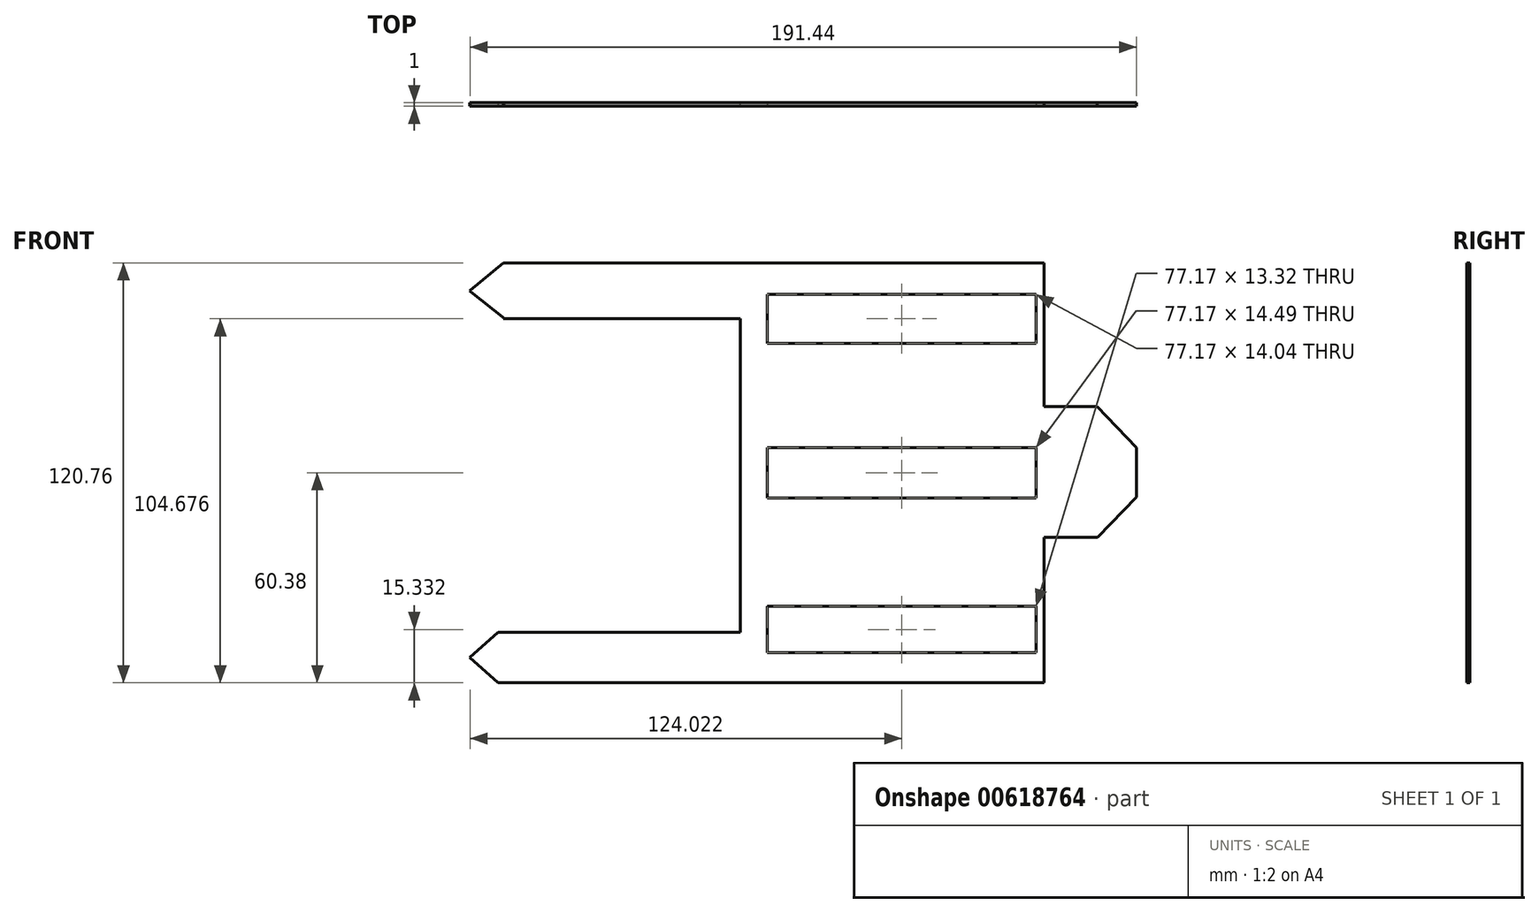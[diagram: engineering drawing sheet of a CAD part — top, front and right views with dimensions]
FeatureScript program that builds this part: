
annotation { "Feature Type Name" : "Feature", "Feature Type Description" : "" }
export const myFeature = defineFeature(function(context is Context, id is Id, definition is map)
    precondition{}
    {
        {
            var Q0;
            Q0=qCreatedBy(makeId("Front.planeOp"),FACE);
            var sketch = newSketch(context, id + "F0", { "sketchPlane" : qUnion([Q0])});
            skLineSegment(sketch, "E0.bottom", {"start": v(95.72, 60.38) * mm, "end": v(-95.72, 60.38) * mm});
            skLineSegment(sketch, "E0.top", {"start": v(95.72, -60.38) * mm, "end": v(-95.72, -60.38) * mm});
            skLineSegment(sketch, "E0.left", {"start": v(95.72, 60.38) * mm, "end": v(95.72, -60.38) * mm});
            skLineSegment(sketch, "E0.right", {"start": v(-95.72, 60.38) * mm, "end": v(-95.72, -60.38) * mm});
            skPoint(sketch, "E0.middle", {"position": v(0, 0) * mm});
            skLineSegment(sketch, "E1", {"start": v(-95.72, 44.3) * mm, "end": v(-18.05, 44.3) * mm});
            skLineSegment(sketch, "E2", {"start": v(-18.05, 44.3) * mm, "end": v(-18.05, -45.81) * mm});
            skLineSegment(sketch, "E3", {"start": v(-18.05, -45.81) * mm, "end": v(-95.72, -45.81) * mm});
            skLineSegment(sketch, "E4", {"start": v(-95.72, -45.81) * mm, "end": v(-95.72, -60.38) * mm});
            skLineSegment(sketch, "E5", {"start": v(-95.72, 44.3) * mm, "end": v(-95.72, 60.38) * mm});
            skLineSegment(sketch, "E6", {"start": v(-95.72, -45.81) * mm, "end": v(-95.72, 44.3) * mm});
            skSolve(sketch);
        }
        {
            var Q0;
            {var subQ1=sQuery(id+"F0.wireOp",EDGE,"E0.bottom");Q0=makeQuery(id+"F0.imprint","IMPRINT",FACE,{"disambiguationData":[TD([[makeQuery(id+"F0.imprint","IMPRINT",EDGE,{"derivedFrom":subQ1}),1.0]])]});}
            extrude(context, id + "F1", {"entities" : qUnion([Q0]), "depth" : 1 * mm, "offsetDistance" : 25.4 * mm});
        }
        {
            var Q0;
            Q0=makeQuery(id+"F1.opExtrude","CAP_FACE",FACE,{"disambiguationData":[OSD([sQuery(id+"F0.wireOp",EDGE,"E0.bottom"),sQuery(id+"F0.wireOp",EDGE,"E0.top"),sQuery(id+"F0.wireOp",EDGE,"E0.left"),sQuery(id+"F0.wireOp",EDGE,"E0.right"),sQuery(id+"F0.wireOp",EDGE,"E1"),sQuery(id+"F0.wireOp",EDGE,"E2"),sQuery(id+"F0.wireOp",EDGE,"E3")])],"isStart":false});
            var sketch = newSketch(context, id + "F2", { "sketchPlane" : qUnion([Q0])});
            skLineSegment(sketch, "E7.bottom", {"start": v(66.89, 7.25) * mm, "end": v(-10.28, 7.25) * mm});
            skLineSegment(sketch, "E7.top", {"start": v(66.89, -7.25) * mm, "end": v(-10.28, -7.25) * mm});
            skLineSegment(sketch, "E7.left", {"start": v(66.89, 7.25) * mm, "end": v(66.89, -7.25) * mm});
            skLineSegment(sketch, "E7.right", {"start": v(-10.28, 7.25) * mm, "end": v(-10.28, -7.25) * mm});
            skPoint(sketch, "E7.middle", {"position": v(28.3, 0) * mm});
            skLineSegment(sketch, "E8.bottom", {"start": v(66.89, -38.39) * mm, "end": v(-10.28, -38.39) * mm});
            skLineSegment(sketch, "E8.top", {"start": v(66.89, -51.7) * mm, "end": v(-10.28, -51.7) * mm});
            skLineSegment(sketch, "E8.left", {"start": v(66.89, -38.39) * mm, "end": v(66.89, -51.7) * mm});
            skLineSegment(sketch, "E8.right", {"start": v(-10.28, -38.39) * mm, "end": v(-10.28, -51.7) * mm});
            skPoint(sketch, "E8.middle", {"position": v(28.3, -45.05) * mm});
            skLineSegment(sketch, "E9.bottom", {"start": v(66.89, 51.32) * mm, "end": v(-10.28, 51.32) * mm});
            skLineSegment(sketch, "E9.top", {"start": v(66.89, 37.28) * mm, "end": v(-10.28, 37.28) * mm});
            skLineSegment(sketch, "E9.left", {"start": v(66.89, 51.32) * mm, "end": v(66.89, 37.28) * mm});
            skLineSegment(sketch, "E9.right", {"start": v(-10.28, 51.32) * mm, "end": v(-10.28, 37.28) * mm});
            skPoint(sketch, "E9.middle", {"position": v(28.3, 44.3) * mm});
            skPoint(sketch, "E9.middle.positionSnap0", {"position": v(28.3, 7.25) * mm});
            skPoint(sketch, "E9.centerSnap0", {"position": v(28.3, 7.25) * mm});
            skSolve(sketch);
        }
        {
            var Q0;
            Q0=makeQuery(id+"F2.imprint","IMPRINT",FACE,{"disambiguationData":[TD([[makeQuery(id+"F2.imprint","IMPRINT",EDGE,{"derivedFrom":sQuery(id+"F2.wireOp",EDGE,"E9.bottom")}),1.0]])]});
            var Q1;
            Q1=makeQuery(id+"F2.imprint","IMPRINT",FACE,{"disambiguationData":[TD([[makeQuery(id+"F2.imprint","IMPRINT",EDGE,{"derivedFrom":sQuery(id+"F2.wireOp",EDGE,"E7.bottom")}),1.0]])]});
            var Q2;
            Q2=makeQuery(id+"F2.imprint","IMPRINT",FACE,{"disambiguationData":[TD([[makeQuery(id+"F2.imprint","IMPRINT",EDGE,{"derivedFrom":sQuery(id+"F2.wireOp",EDGE,"E8.bottom")}),1.0]])]});
            extrude(context, id + "F3", {"entities" : qUnion([Q0, Q1, Q2]), "operationType" : NewBodyOperationType.REMOVE, "oppositeDirection" : true, "depth" : 25.4 * mm, "offsetDistance" : 25.4 * mm});
        }
        {
            var Q0;
            Q0=makeQuery(id+"F1.opExtrude","CAP_FACE",FACE,{"disambiguationData":[OSD([sQuery(id+"F0.wireOp",EDGE,"E0.bottom"),sQuery(id+"F0.wireOp",EDGE,"E0.top"),sQuery(id+"F0.wireOp",EDGE,"E0.left"),sQuery(id+"F0.wireOp",EDGE,"E0.right"),sQuery(id+"F0.wireOp",EDGE,"E1"),sQuery(id+"F0.wireOp",EDGE,"E2"),sQuery(id+"F0.wireOp",EDGE,"E3")])],"isStart":false});
            var sketch = newSketch(context, id + "F4", { "sketchPlane" : qUnion([Q0])});
            skLineSegment(sketch, "E10", {"start": v(69.14, 0) * mm, "end": v(69.14, -18.59) * mm});
            skLineSegment(sketch, "E11", {"start": v(69.14, -18.59) * mm, "end": v(84.5, -18.59) * mm});
            skLineSegment(sketch, "E12", {"start": v(69.14, 0) * mm, "end": v(69.14, 19.07) * mm});
            skLineSegment(sketch, "E13", {"start": v(69.14, 19.07) * mm, "end": v(84.46, 19.07) * mm});
            skLineSegment(sketch, "E14", {"start": v(84.46, 19.07) * mm, "end": v(95.72, 7.22) * mm});
            skLineSegment(sketch, "E15", {"start": v(95.72, 7.22) * mm, "end": v(95.72, -7) * mm});
            skLineSegment(sketch, "E16", {"start": v(95.72, -7) * mm, "end": v(84.5, -18.59) * mm});
            skLineSegment(sketch, "E17", {"start": v(69.14, 19.07) * mm, "end": v(69.14, 60.38) * mm});
            skLineSegment(sketch, "E18", {"start": v(69.14, 60.38) * mm, "end": v(95.72, 60.38) * mm});
            skLineSegment(sketch, "E19", {"start": v(95.72, 60.38) * mm, "end": v(95.72, 7.22) * mm});
            skLineSegment(sketch, "E20", {"start": v(69.14, -18.59) * mm, "end": v(69.14, -60.38) * mm});
            skLineSegment(sketch, "E21", {"start": v(69.14, -60.38) * mm, "end": v(95.72, -60.38) * mm});
            skLineSegment(sketch, "E22", {"start": v(95.72, -60.38) * mm, "end": v(95.72, -7) * mm});
            skSolve(sketch);
        }
        {
            var Q0;
            Q0=makeQuery(id+"F4.imprint","IMPRINT",FACE,{"disambiguationData":[TD([[makeQuery(id+"F4.imprint","IMPRINT",EDGE,{"derivedFrom":sQuery(id+"F4.wireOp",EDGE,"E11")}),-1.0]])]});
            var Q1;
            Q1=makeQuery(id+"F4.imprint","IMPRINT",FACE,{"disambiguationData":[TD([[makeQuery(id+"F4.imprint","IMPRINT",EDGE,{"derivedFrom":sQuery(id+"F4.wireOp",EDGE,"E13")}),1.0]])]});
            extrude(context, id + "F5", {"entities" : qUnion([Q0, Q1]), "operationType" : NewBodyOperationType.REMOVE, "oppositeDirection" : true, "depth" : 25.4 * mm, "offsetDistance" : 25.4 * mm});
        }
        {
            var Q0;
            Q0=makeQuery(id+"F1.opExtrude","CAP_FACE",FACE,{"disambiguationData":[OSD([sQuery(id+"F0.wireOp",EDGE,"E0.bottom"),sQuery(id+"F0.wireOp",EDGE,"E0.top"),sQuery(id+"F0.wireOp",EDGE,"E0.left"),sQuery(id+"F0.wireOp",EDGE,"E0.right"),sQuery(id+"F0.wireOp",EDGE,"E1"),sQuery(id+"F0.wireOp",EDGE,"E2"),sQuery(id+"F0.wireOp",EDGE,"E3")])],"isStart":false});
            var sketch = newSketch(context, id + "F6", { "sketchPlane" : qUnion([Q0])});
            skLineSegment(sketch, "E23", {"start": v(-95.72, 52.34) * mm, "end": v(-88.4, 60.38) * mm});
            skLineSegment(sketch, "E24", {"start": v(-88.4, 60.38) * mm, "end": v(-88.4, 44.3) * mm});
            skLineSegment(sketch, "E25", {"start": v(-88.4, 44.3) * mm, "end": v(-95.72, 52.34) * mm});
            skLineSegment(sketch, "E26", {"start": v(-95.72, 52.34) * mm, "end": v(-95.72, 44.3) * mm});
            skLineSegment(sketch, "E27", {"start": v(-95.72, 44.3) * mm, "end": v(-88.4, 44.3) * mm});
            skLineSegment(sketch, "E28", {"start": v(-88.4, 60.38) * mm, "end": v(-95.72, 60.38) * mm});
            skLineSegment(sketch, "E29", {"start": v(-95.72, 60.38) * mm, "end": v(-95.72, 52.34) * mm});
            skSolve(sketch);
        }
        {
            var Q0;
            Q0=makeQuery(id+"F6.imprint","IMPRINT",FACE,{"disambiguationData":[TD([[makeQuery(id+"F6.imprint","IMPRINT",EDGE,{"derivedFrom":sQuery(id+"F6.wireOp",EDGE,"E23")}),1.0]])]});
            var Q1;
            Q1=makeQuery(id+"F6.imprint","IMPRINT",FACE,{"disambiguationData":[TD([[makeQuery(id+"F6.imprint","IMPRINT",EDGE,{"derivedFrom":sQuery(id+"F6.wireOp",EDGE,"E25")}),1.0]])]});
            extrude(context, id + "F7", {"entities" : qUnion([Q0, Q1]), "operationType" : NewBodyOperationType.REMOVE, "oppositeDirection" : true, "depth" : 25.4 * mm, "offsetDistance" : 25.4 * mm});
        }
        {
            var Q0;
            Q0=makeQuery(id+"F1.opExtrude","CAP_FACE",FACE,{"disambiguationData":[OSD([sQuery(id+"F0.wireOp",EDGE,"E0.bottom"),sQuery(id+"F0.wireOp",EDGE,"E0.top"),sQuery(id+"F0.wireOp",EDGE,"E0.left"),sQuery(id+"F0.wireOp",EDGE,"E0.right"),sQuery(id+"F0.wireOp",EDGE,"E1"),sQuery(id+"F0.wireOp",EDGE,"E2"),sQuery(id+"F0.wireOp",EDGE,"E3")])],"isStart":false});
            var sketch = newSketch(context, id + "F8", { "sketchPlane" : qUnion([Q0])});
            skLineSegment(sketch, "E30", {"start": v(-95.72, -53.1) * mm, "end": v(-87.66, -45.81) * mm});
            skLineSegment(sketch, "E31", {"start": v(-87.66, -45.81) * mm, "end": v(-87.66, -60.38) * mm});
            skLineSegment(sketch, "E32", {"start": v(-87.66, -60.38) * mm, "end": v(-95.72, -53.1) * mm});
            skLineSegment(sketch, "E33", {"start": v(-87.66, -45.81) * mm, "end": v(-95.72, -45.81) * mm});
            skLineSegment(sketch, "E34", {"start": v(-95.72, -45.81) * mm, "end": v(-95.72, -53.1) * mm});
            skLineSegment(sketch, "E35", {"start": v(-87.66, -60.38) * mm, "end": v(-95.72, -60.38) * mm});
            skLineSegment(sketch, "E36", {"start": v(-95.72, -60.38) * mm, "end": v(-95.72, -53.1) * mm});
            skSolve(sketch);
        }
        {
            var Q0;
            Q0=makeQuery(id+"F8.imprint","IMPRINT",FACE,{"disambiguationData":[TD([[makeQuery(id+"F8.imprint","IMPRINT",EDGE,{"derivedFrom":sQuery(id+"F8.wireOp",EDGE,"E30")}),1.0]])]});
            var Q1;
            Q1=makeQuery(id+"F8.imprint","IMPRINT",FACE,{"disambiguationData":[TD([[makeQuery(id+"F8.imprint","IMPRINT",EDGE,{"derivedFrom":sQuery(id+"F8.wireOp",EDGE,"E32")}),1.0]])]});
            extrude(context, id + "F9", {"entities" : qUnion([Q0, Q1]), "operationType" : NewBodyOperationType.REMOVE, "oppositeDirection" : true, "depth" : 25.4 * mm, "offsetDistance" : 25.4 * mm});
        }
        {
            var Q0;
            Q0=makeQuery(id+"F1.opExtrude","CAP_FACE",FACE,{"disambiguationData":[OSD([sQuery(id+"F0.wireOp",EDGE,"E0.bottom"),sQuery(id+"F0.wireOp",EDGE,"E0.top"),sQuery(id+"F0.wireOp",EDGE,"E0.left"),sQuery(id+"F0.wireOp",EDGE,"E0.right"),sQuery(id+"F0.wireOp",EDGE,"E1"),sQuery(id+"F0.wireOp",EDGE,"E2"),sQuery(id+"F0.wireOp",EDGE,"E3")])],"isStart":false});
            var sketch = newSketch(context, id + "F10", { "sketchPlane" : qUnion([Q0])});
            skLineSegment(sketch, "E37", {"start": v(-95.72, -53.1) * mm, "end": v(-87.66, -53.1) * mm});
            skLineSegment(sketch, "E38", {"start": v(-95.72, 52.34) * mm, "end": v(-87.61, 52.34) * mm});
            skSolve(sketch);
        }
        {
            var Q0;
            Q0=makeQuery(id+"F10.imprint","IMPRINT",FACE,{"disambiguationData":[TD([[makeQuery(id+"F10.imprint","IMPRINT",EDGE,{"derivedFrom":makeQuery(id+"F1.opExtrude","CAP_EDGE",EDGE,{"disambiguationData":[OSD([sQuery(id+"F0.wireOp",EDGE,"E2")])],"isStart":false})}),1.0]])]});
            var sketch = newSketch(context, id + "F11", { "sketchPlane" : qUnion([Q0])});
            skLineSegment(sketch, "E39", {"start": v(-96, 52.52) * mm, "end": v(-85.7, 44.32) * mm});
            skLineSegment(sketch, "E40", {"start": v(-85.7, 44.32) * mm, "end": v(-89.33, 44.32) * mm});
            skLineSegment(sketch, "E41", {"start": v(-89.33, 44.32) * mm, "end": v(-96, 52.52) * mm});
            skLineSegment(sketch, "E42", {"start": v(-96, 52.52) * mm, "end": v(-87.52, 59.44) * mm});
            skPoint(sketch, "E42.endSnap0", {"position": v(-87.52, 44.32) * mm});
            skLineSegment(sketch, "E43", {"start": v(-87.52, 59.44) * mm, "end": v(-89.33, 61.66) * mm});
            skLineSegment(sketch, "E44", {"start": v(-89.33, 61.66) * mm, "end": v(-96, 52.52) * mm});
            skSolve(sketch);
        }
        {
            var Q0;
            {var subQ0=sQuery(id+"F11.wireOp",EDGE,"E40");var subQ1=sQuery(id+"F11.wireOp",EDGE,"E39");var subQ2=makeQuery(id+"F11.imprint","INTERSECT",VERTEX,{"derivedFrom":[subQ1,subQ0]});Q0=makeQuery(id+"F11.imprint","IMPRINT",FACE,{"disambiguationData":[TD([[makeQuery(id+"F11.imprint","IMPRINT",EDGE,{"disambiguationData":[TD([[subQ2,1.0]])],"derivedFrom":subQ1}),-1.0]])]});}
            var Q1;
            {var subQ0=sQuery(id+"F11.wireOp",EDGE,"E43");var subQ1=sQuery(id+"F11.wireOp",EDGE,"E42");var subQ2=makeQuery(id+"F11.imprint","INTERSECT",VERTEX,{"derivedFrom":[subQ1,subQ0]});Q1=makeQuery(id+"F11.imprint","IMPRINT",FACE,{"disambiguationData":[TD([[makeQuery(id+"F11.imprint","IMPRINT",EDGE,{"disambiguationData":[TD([[subQ2,1.0]])],"derivedFrom":subQ1}),1.0]])]});}
            extrude(context, id + "F12", {"entities" : qUnion([Q0, Q1]), "operationType" : NewBodyOperationType.REMOVE, "oppositeDirection" : true, "depth" : 25.4 * mm, "offsetDistance" : 25.4 * mm});
        }
        {
            var Q0;
            Q0=makeQuery(id+"F10.imprint","IMPRINT",FACE,{"disambiguationData":[TD([[makeQuery(id+"F10.imprint","IMPRINT",EDGE,{"derivedFrom":makeQuery(id+"F1.opExtrude","CAP_EDGE",EDGE,{"disambiguationData":[OSD([sQuery(id+"F0.wireOp",EDGE,"E2")])],"isStart":false})}),1.0]])]});
            var sketch = newSketch(context, id + "F13", { "sketchPlane" : qUnion([Q0])});
            skLineSegment(sketch, "E45", {"start": v(-95.75, 52.33) * mm, "end": v(-86.06, 60.44) * mm});
            skLineSegment(sketch, "E46", {"start": v(-86.06, 60.44) * mm, "end": v(-86.06, 44.26) * mm});
            skLineSegment(sketch, "E47", {"start": v(-86.06, 44.26) * mm, "end": v(-95.75, 52.33) * mm});
            skLineSegment(sketch, "E48", {"start": v(-95.75, 52.33) * mm, "end": v(-94.14, 54.27) * mm});
            skLineSegment(sketch, "E49", {"start": v(-94.14, 54.27) * mm, "end": v(-87.62, 59.72) * mm});
            skSolve(sketch);
        }
        {
            var Q0;
            {var subQ0=sQuery(id+"F13.wireOp",EDGE,"E45");var subQ1=makeQuery(id+"F10.imprint","IMPRINT",EDGE,{"derivedFrom":makeQuery(id+"F1.opExtrude","CAP_EDGE",EDGE,{"disambiguationData":[OSD([sQuery(id+"F0.wireOp",EDGE,"E0.bottom")])],"isStart":false})});var subQ2=makeQuery(id+"F13.imprint","INTERSECT",VERTEX,{"derivedFrom":[subQ1,subQ0]});Q0=makeQuery(id+"F13.imprint","IMPRINT",FACE,{"disambiguationData":[TD([[makeQuery(id+"F13.imprint","IMPRINT",EDGE,{"disambiguationData":[TD([[subQ2,1.0]])],"derivedFrom":subQ0}),1.0]])]});}
            var Q1;
            {var subQ0=sQuery(id+"F13.wireOp",EDGE,"E47");var subQ1=makeQuery(id+"F10.imprint","IMPRINT",EDGE,{"derivedFrom":makeQuery(id+"F1.opExtrude","CAP_EDGE",EDGE,{"disambiguationData":[OSD([sQuery(id+"F0.wireOp",EDGE,"E1")])],"isStart":false})});var subQ2=makeQuery(id+"F13.imprint","INTERSECT",VERTEX,{"derivedFrom":[subQ1,subQ0]});Q1=makeQuery(id+"F13.imprint","IMPRINT",FACE,{"disambiguationData":[TD([[makeQuery(id+"F13.imprint","IMPRINT",EDGE,{"disambiguationData":[TD([[subQ2,-1.0]])],"derivedFrom":subQ0}),1.0]])]});}
            extrude(context, id + "F14", {"entities" : qUnion([Q0, Q1]), "operationType" : NewBodyOperationType.REMOVE, "oppositeDirection" : true, "depth" : 25.4 * mm, "offsetDistance" : 25.4 * mm});
        }
    });
